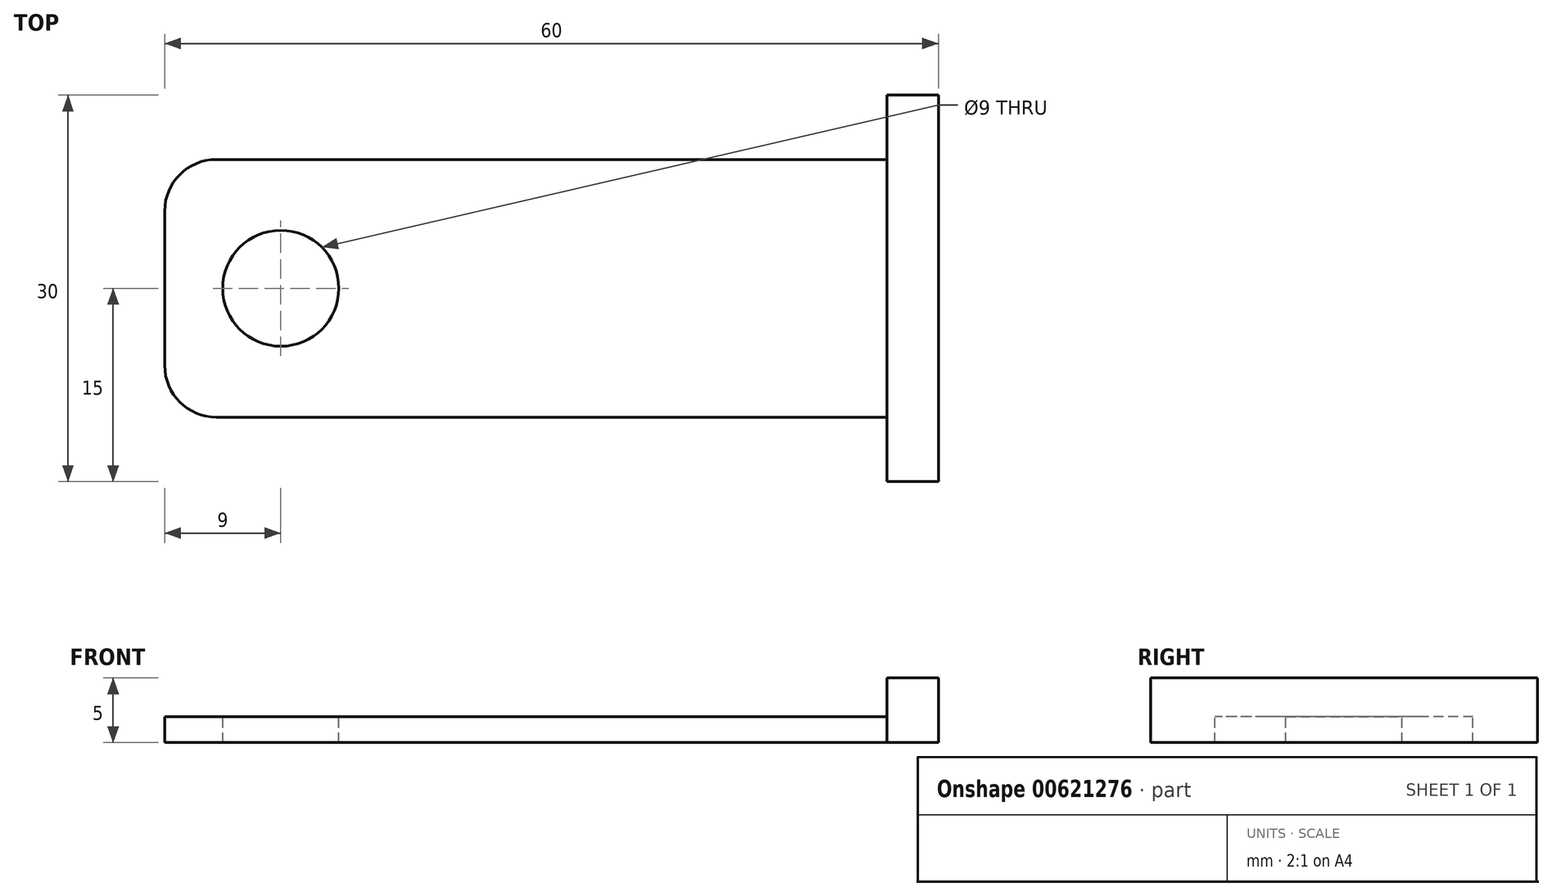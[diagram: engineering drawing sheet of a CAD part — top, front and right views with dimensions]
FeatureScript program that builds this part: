
annotation { "Feature Type Name" : "Feature", "Feature Type Description" : "" }
export const myFeature = defineFeature(function(context is Context, id is Id, definition is map)
    precondition{}
    {
        {
            var Q0;
            Q0=qCreatedBy(makeId("Top.planeOp"),FACE);
            var sketch = newSketch(context, id + "F0", { "sketchPlane" : qUnion([Q0])});
            skLineSegment(sketch, "E0.bottom", {"start": v(28, 10) * mm, "end": v(-28, 10) * mm});
            skLineSegment(sketch, "E0.top", {"start": v(28, -10) * mm, "end": v(-28, -10) * mm});
            skLineSegment(sketch, "E0.left", {"start": v(28, 10) * mm, "end": v(28, -10) * mm});
            skLineSegment(sketch, "E0.right", {"start": v(-28, 10) * mm, "end": v(-28, -10) * mm});
            skPoint(sketch, "E0.middle", {"position": v(0, 0) * mm});
            skLineSegment(sketch, "E1.bottom", {"start": v(28, 15) * mm, "end": v(32, 15) * mm});
            skLineSegment(sketch, "E1.top", {"start": v(28, -15) * mm, "end": v(32, -15) * mm});
            skLineSegment(sketch, "E1.left", {"start": v(28, 15) * mm, "end": v(28, -15) * mm});
            skLineSegment(sketch, "E1.right", {"start": v(32, 15) * mm, "end": v(32, -15) * mm});
            skPoint(sketch, "E1.middle", {"position": v(30, 0) * mm});
            skPoint(sketch, "E1.middle.positionSnap0", {"position": v(28, 0) * mm});
            skPoint(sketch, "E1.centerSnap0", {"position": v(28, 0) * mm});
            skCircle(sketch, "E2", {"center": v(-19, 0) * mm, "radius": 4.5 * mm});
            skSolve(sketch);
        }
        {
            var Q0;
            {var subQ3=sQuery(id+"F0.wireOp",EDGE,"E1.bottom");Q0=makeQuery(id+"F0.imprint","IMPRINT",FACE,{"disambiguationData":[TD([[makeQuery(id+"F0.imprint","IMPRINT",EDGE,{"derivedFrom":subQ3}),-1.0]])]});}
            extrude(context, id + "F1", {"entities" : qUnion([Q0]), "depth" : 4 * mm, "offsetDistance" : 25 * mm, "hasSecondDirection" : true, "secondDirectionOppositeDirection" : true, "secondDirectionDepth" : 1 * mm});
        }
        {
            var Q0;
            {var subQ1=sQuery(id+"F0.wireOp",EDGE,"E0.bottom");Q0=makeQuery(id+"F0.imprint","IMPRINT",FACE,{"disambiguationData":[TD([[makeQuery(id+"F0.imprint","IMPRINT",EDGE,{"derivedFrom":subQ1}),1.0]])]});}
            extrude(context, id + "F2", {"entities" : qUnion([Q0]), "endBound" : BoundingType.SYMMETRIC, "oppositeDirection" : true, "depth" : 2 * mm, "offsetDistance" : 25 * mm});
        }
        {
            var Q0;
            Q0=makeQuery(id+"F2.opExtrude","SWEPT_EDGE",EDGE,{"disambiguationData":[OSD([sQuery(id+"F0.wireOp",EDGE,"E0.top"),sQuery(id+"F0.wireOp",EDGE,"E0.right")])]});
            fillet(context, id + "F3", {"entities" : qUnion([Q0]), "radius" : 4 * mm, "tangentPropagation" : true, "allowEdgeOverflow" : false});
        }
        {
            var Q0;
            Q0=makeQuery(id+"F2.opExtrude","SWEPT_EDGE",EDGE,{"disambiguationData":[OSD([sQuery(id+"F0.wireOp",EDGE,"E0.bottom"),sQuery(id+"F0.wireOp",EDGE,"E0.right")])]});
            fillet(context, id + "F4", {"entities" : qUnion([Q0]), "radius" : 4 * mm, "tangentPropagation" : true, "allowEdgeOverflow" : false});
        }
    });
